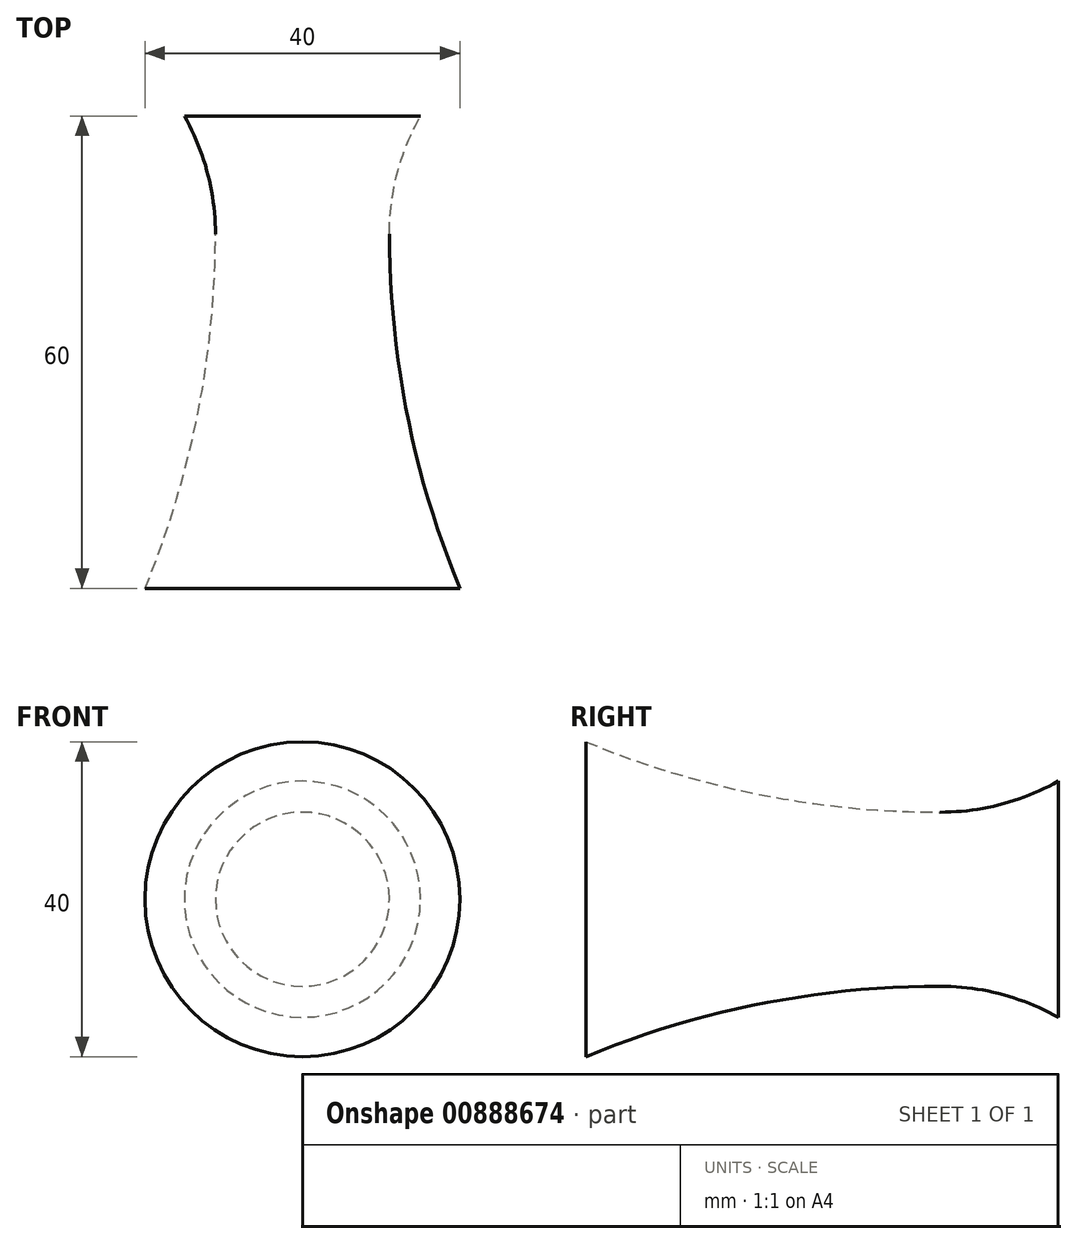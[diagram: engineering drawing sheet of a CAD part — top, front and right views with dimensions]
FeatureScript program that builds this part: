
annotation { "Feature Type Name" : "Feature", "Feature Type Description" : "" }
export const myFeature = defineFeature(function(context is Context, id is Id, definition is map)
    precondition{}
    {
        {
            var Q0;
            Q0=qCreatedBy(makeId("Top.planeOp"),FACE);
            var sketch = newSketch(context, id + "F0", { "sketchPlane" : qUnion([Q0])});
            skLineSegment(sketch, "E0", {"start": v(0, 0) * mm, "end": v(20, 0) * mm});
            skArc(sketch, "E1", {"start": v(11.05, 45) * mm, "mid": v(13.31, 22.06) * mm, "end": v(20, 0) * mm});
            skLineSegment(sketch, "E2", {"start": v(0, 0) * mm, "end": v(0, 60) * mm});
            skLineSegment(sketch, "E3", {"start": v(0, 60) * mm, "end": v(15, 60) * mm});
            skArc(sketch, "E4", {"start": v(15, 60) * mm, "mid": v(12.06, 52.76) * mm, "end": v(11.05, 45) * mm});
            skLineSegment(sketch, "E5", {"start": v(11.05, 45) * mm, "end": v(11.05, 24.09) * mm, "construction": true});
            skSolve(sketch);
        }
        {
            var Q0;
            Q0=makeQuery(id+"F0.imprint","IMPRINT",FACE,{"disambiguationData":[TD([[makeQuery(id+"F0.imprint","IMPRINT",EDGE,{"derivedFrom":sQuery(id+"F0.wireOp",EDGE,"E0")}),1.0]])]});
            var Q1;
            Q1=sQuery(id+"F0.wireOp",EDGE,"E2");
            revolve(context, id + "F1", {"surfaceOperationType" : NewSurfaceOperationType.NEW, "entities" : qUnion([Q0]), "axis" : qUnion([Q1]), "revolveType" : RevolveType.FULL});
        }
    });
